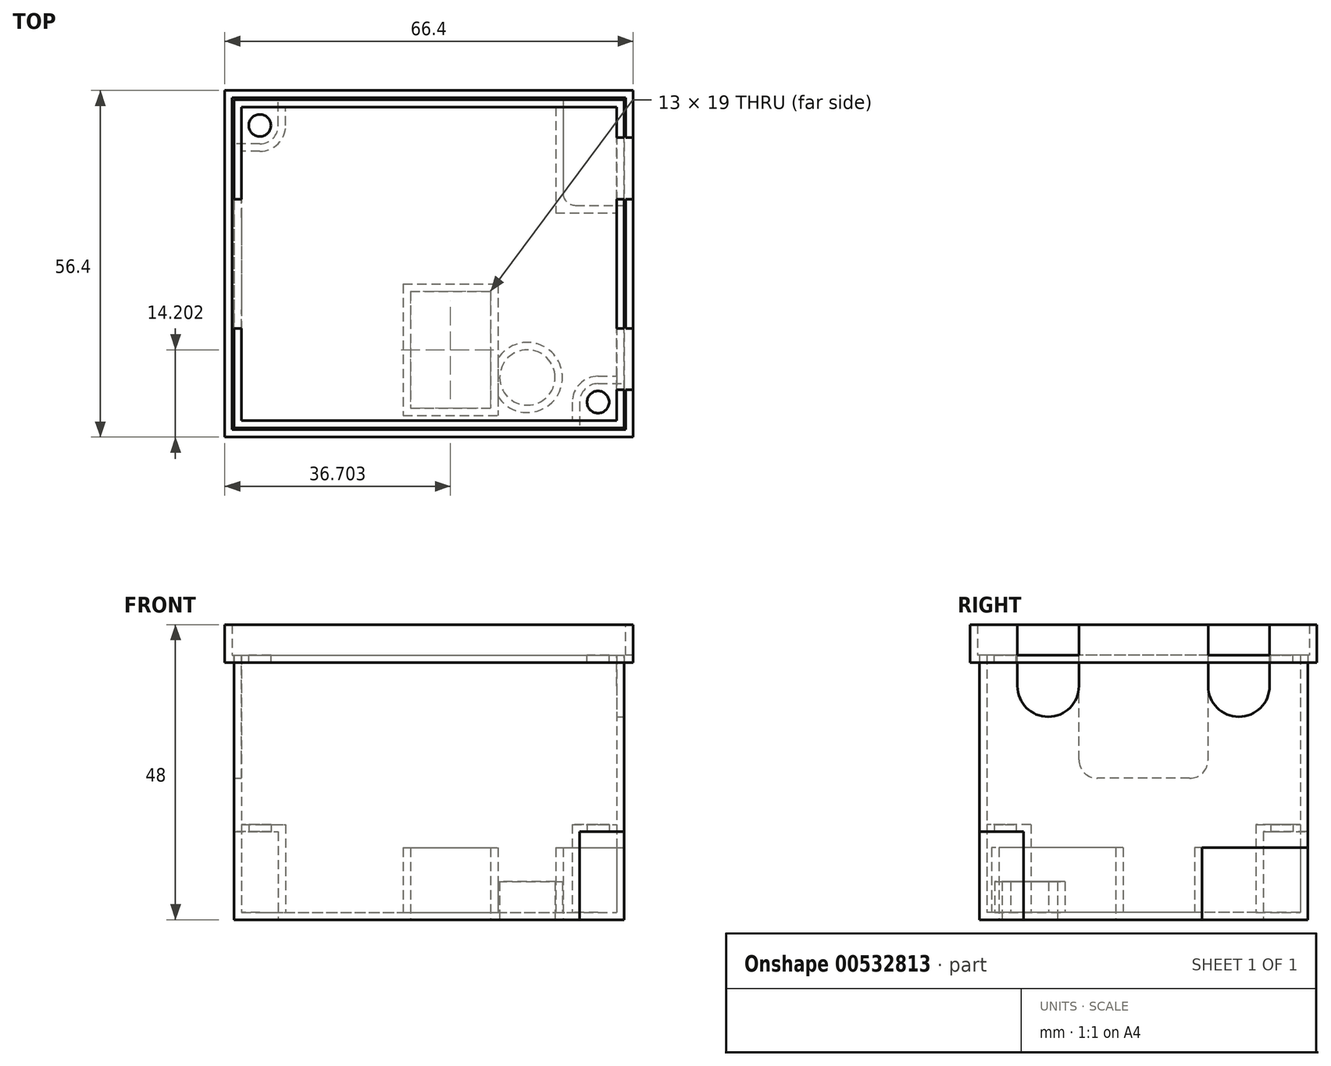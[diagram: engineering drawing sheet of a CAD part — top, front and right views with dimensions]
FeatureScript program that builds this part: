
annotation { "Feature Type Name" : "Feature", "Feature Type Description" : "" }
export const myFeature = defineFeature(function(context is Context, id is Id, definition is map)
    precondition{}
    {
        {
            var Q0;
            Q0=qCreatedBy(makeId("Top.planeOp"),FACE);
            var sketch = newSketch(context, id + "F0", { "sketchPlane" : qUnion([Q0])});
            skLineSegment(sketch, "E0.bottom", {"start": v(-16.96, 26.85) * mm, "end": v(46.44, 26.85) * mm});
            skLineSegment(sketch, "E0.top", {"start": v(-16.96, -26.55) * mm, "end": v(46.44, -26.55) * mm});
            skLineSegment(sketch, "E0.left", {"start": v(-16.96, 26.85) * mm, "end": v(-16.96, -26.55) * mm});
            skLineSegment(sketch, "E0.right", {"start": v(46.44, 26.85) * mm, "end": v(46.44, -26.55) * mm});
            skCircle(sketch, "E1", {"center": v(30.74, -18.35) * mm, "radius": 4.5 * mm});
            skLineSegment(sketch, "E2.bottom", {"start": v(11.74, -4.35) * mm, "end": v(24.74, -4.35) * mm});
            skLineSegment(sketch, "E2.top", {"start": v(11.74, -23.35) * mm, "end": v(24.74, -23.35) * mm});
            skLineSegment(sketch, "E2.left", {"start": v(11.74, -4.35) * mm, "end": v(11.74, -23.35) * mm});
            skLineSegment(sketch, "E2.right", {"start": v(24.74, -4.35) * mm, "end": v(24.74, -23.35) * mm});
            skArc(sketch, "E3", {"start": v(42.24, -19.35) * mm, "mid": v(40.12, -20.23) * mm, "end": v(39.24, -22.35) * mm});
            skArc(sketch, "E4", {"start": v(-12.76, 19.65) * mm, "mid": v(-10.64, 20.53) * mm, "end": v(-9.76, 22.65) * mm});
            skLineSegment(sketch, "E5", {"start": v(-12.76, 19.65) * mm, "end": v(-16.96, 19.65) * mm});
            skLineSegment(sketch, "E6", {"start": v(-9.76, 22.65) * mm, "end": v(-9.76, 26.85) * mm});
            skCircle(sketch, "E7", {"center": v(-12.76, 22.65) * mm, "radius": 1.8 * mm});
            skLineSegment(sketch, "E8", {"start": v(36.54, 26.85) * mm, "end": v(36.54, 9.65) * mm});
            skLineSegment(sketch, "E9", {"start": v(36.54, 9.65) * mm, "end": v(46.44, 9.65) * mm});
            skLineSegment(sketch, "E10", {"start": v(42.24, -19.35) * mm, "end": v(46.44, -19.35) * mm});
            skLineSegment(sketch, "E11", {"start": v(39.24, -22.35) * mm, "end": v(39.24, -26.55) * mm});
            skCircle(sketch, "E12", {"center": v(42.24, -22.35) * mm, "radius": 1.8 * mm});
            skSolve(sketch);
        }
        {
            var Q0;
            Q0=makeQuery(id+"F0.imprint","IMPRINT",FACE,{"disambiguationData":[TD([[makeQuery(id+"F0.imprint","IMPRINT",EDGE,{"derivedFrom":sQuery(id+"F0.wireOp",EDGE,"E0.bottom")}),-1.0]])]});
            var Q1;
            Q1=makeQuery(id+"F0.imprint","IMPRINT",FACE,{"disambiguationData":[TD([[makeQuery(id+"F0.imprint","IMPRINT",EDGE,{"derivedFrom":sQuery(id+"F0.wireOp",EDGE,"9tdKmkdn-hE9F-qVrS-l7sH-JdWV1MObEDVF.bottom")}),-1.0]])]});
            var Q2;
            Q2=makeQuery(id+"F0.imprint","IMPRINT",FACE,{"disambiguationData":[TD([[makeQuery(id+"F0.imprint","IMPRINT",EDGE,{"derivedFrom":sQuery(id+"F0.wireOp",EDGE,"E2.bottom")}),-1.0]])]});
            var Q3;
            Q3=makeQuery(id+"F0.imprint","IMPRINT",FACE,{"disambiguationData":[TD([[makeQuery(id+"F0.imprint","IMPRINT",EDGE,{"derivedFrom":sQuery(id+"F0.wireOp",EDGE,"E1")}),1.0]])]});
            var Q4;
            Q4=makeQuery(id+"F0.imprint","IMPRINT",FACE,{"disambiguationData":[TD([[makeQuery(id+"F0.imprint","IMPRINT",EDGE,{"derivedFrom":sQuery(id+"F0.wireOp",EDGE,"E4")}),1.0]])]});
            var Q5;
            Q5=makeQuery(id+"F0.imprint","IMPRINT",FACE,{"disambiguationData":[TD([[makeQuery(id+"F0.imprint","IMPRINT",EDGE,{"derivedFrom":sQuery(id+"F0.wireOp",EDGE,"E3")}),1.0]])]});
            var Q6;
            Q6=makeQuery(id+"F0.imprint","IMPRINT",FACE,{"disambiguationData":[TD([[makeQuery(id+"F0.imprint","IMPRINT",EDGE,{"derivedFrom":sQuery(id+"F0.wireOp",EDGE,"E1")}),-1.0]])]});
            var Q7;
            Q7=makeQuery(id+"F0.imprint","IMPRINT",FACE,{"disambiguationData":[TD([[makeQuery(id+"F0.imprint","IMPRINT",EDGE,{"derivedFrom":sQuery(id+"F0.wireOp",EDGE,"E7")}),1.0]])]});
            var Q8;
            Q8=makeQuery(id+"F0.imprint","IMPRINT",FACE,{"disambiguationData":[TD([[makeQuery(id+"F0.imprint","IMPRINT",EDGE,{"derivedFrom":sQuery(id+"F0.wireOp",EDGE,"E12")}),1.0]])]});
            extrude(context, id + "F1", {"entities" : qUnion([Q0, Q1, Q2, Q3, Q4, Q5, Q6, Q7, Q8]), "depth" : 43 * mm, "offsetDistance" : 25 * mm});
        }
        {
            var Q0;
            Q0=makeQuery(id+"F0.imprint","IMPRINT",FACE,{"disambiguationData":[TD([[makeQuery(id+"F0.imprint","IMPRINT",EDGE,{"derivedFrom":sQuery(id+"F0.wireOp",EDGE,"E2.bottom")}),-1.0]])]});
            extrude(context, id + "F2", {"entities" : qUnion([Q0]), "operationType" : NewBodyOperationType.REMOVE, "depth" : 10.5 * mm, "offsetDistance" : 25 * mm});
        }
        {
            var Q0;
            {var subQ3=sQuery(id+"F0.wireOp",EDGE,"E8");Q0=makeQuery(id+"F0.imprint","IMPRINT",FACE,{"disambiguationData":[TD([[makeQuery(id+"F0.imprint","IMPRINT",EDGE,{"derivedFrom":subQ3}),1.0]])]});}
            extrude(context, id + "F3", {"entities" : qUnion([Q0]), "operationType" : NewBodyOperationType.REMOVE, "depth" : 10.5 * mm, "offsetDistance" : 25 * mm});
        }
        {
            var Q0;
            Q0=makeQuery(id+"F0.imprint","IMPRINT",FACE,{"disambiguationData":[TD([[makeQuery(id+"F0.imprint","IMPRINT",EDGE,{"derivedFrom":sQuery(id+"F0.wireOp",EDGE,"E1")}),1.0]])]});
            extrude(context, id + "F4", {"entities" : qUnion([Q0]), "operationType" : NewBodyOperationType.REMOVE, "depth" : 5 * mm, "offsetDistance" : 25 * mm});
        }
        {
            var Q0;
            Q0=makeQuery(id+"F0.imprint","IMPRINT",FACE,{"disambiguationData":[TD([[makeQuery(id+"F0.imprint","IMPRINT",EDGE,{"derivedFrom":sQuery(id+"F0.wireOp",EDGE,"E3")}),1.0]])]});
            var Q1;
            Q1=makeQuery(id+"F0.imprint","IMPRINT",FACE,{"disambiguationData":[TD([[makeQuery(id+"F0.imprint","IMPRINT",EDGE,{"derivedFrom":sQuery(id+"F0.wireOp",EDGE,"E4")}),1.0]])]});
            var Q2;
            Q2=makeQuery(id+"F0.imprint","IMPRINT",FACE,{"disambiguationData":[TD([[makeQuery(id+"F0.imprint","IMPRINT",EDGE,{"derivedFrom":sQuery(id+"F0.wireOp",EDGE,"E12")}),1.0]])]});
            var Q3;
            Q3=makeQuery(id+"F0.imprint","IMPRINT",FACE,{"disambiguationData":[TD([[makeQuery(id+"F0.imprint","IMPRINT",EDGE,{"derivedFrom":sQuery(id+"F0.wireOp",EDGE,"E7")}),1.0]])]});
            extrude(context, id + "F5", {"entities" : qUnion([Q0, Q1, Q2, Q3]), "operationType" : NewBodyOperationType.REMOVE, "depth" : 14.3 * mm, "offsetDistance" : 25 * mm});
        }
        {
            var Q0;
            Q0=makeQuery(id+"F1.opExtrude","CAP_FACE",FACE,{"disambiguationData":[OSD([sQuery(id+"F0.wireOp",EDGE,"E0.bottom"),sQuery(id+"F0.wireOp",EDGE,"E0.top"),sQuery(id+"F0.wireOp",EDGE,"E0.left"),sQuery(id+"F0.wireOp",EDGE,"E0.right"),sQuery(id+"F0.wireOp",EDGE,"9tdKmkdn-hE9F-qVrS-l7sH-JdWV1MObEDVF.bottom"),sQuery(id+"F0.wireOp",EDGE,"9tdKmkdn-hE9F-qVrS-l7sH-JdWV1MObEDVF.left")])],"isStart":false});
            shell(context, id + "F6", {"entities" : qUnion([Q0]), "thickness" : 1.2 * mm});
        }
        {
            var Q0;
            Q0=makeQuery(id+"F3.boolean.opBoolean","COPY",FACE,{"derivedFrom":makeQuery(id+"F3.opExtrude","CAP_FACE",FACE,{"disambiguationData":[OSD([sQuery(id+"F0.wireOp",EDGE,"E0.bottom"),sQuery(id+"F0.wireOp",EDGE,"E0.right"),sQuery(id+"F0.wireOp",EDGE,"E8"),sQuery(id+"F0.wireOp",EDGE,"E9")])],"isStart":false})});
            extrude(context, id + "F7", {"entities" : qUnion([Q0]), "operationType" : NewBodyOperationType.REMOVE, "oppositeDirection" : true, "depth" : 1.2 * mm, "offsetDistance" : 25 * mm});
        }
        {
            var Q0;
            {var subQ0=sQuery(id+"F0.wireOp",EDGE,"E9");var subQ1=sQuery(id+"F0.wireOp",EDGE,"E8");Q0=makeQuery(id+"F7.boolean.opBoolean","MERGE",EDGE,{"derivedFrom":[makeQuery(id+"F3.boolean.opBoolean","COPY",EDGE,{"derivedFrom":makeQuery(id+"F3.opExtrude","SWEPT_EDGE",EDGE,{"disambiguationData":[OSD([subQ1,subQ0])]})}),makeQuery(id+"F7.opExtrude","SWEPT_EDGE",EDGE,{"disambiguationData":[OSD([subQ1,subQ0])]})]});}
            var Q1;
            {var subQ0=sQuery(id+"F0.wireOp",EDGE,"E8");var subQ1=sQuery(id+"F0.wireOp",EDGE,"E0.bottom");Q1=makeQuery(id+"F7.boolean.opBoolean","MERGE",EDGE,{"derivedFrom":[makeQuery(id+"F3.boolean.opBoolean","COPY",EDGE,{"derivedFrom":makeQuery(id+"F3.opExtrude","SWEPT_EDGE",EDGE,{"disambiguationData":[OSD([subQ1,subQ0])]})}),makeQuery(id+"F7.opExtrude","SWEPT_EDGE",EDGE,{"disambiguationData":[OSD([subQ1,subQ0])]})]});}
            var Q2;
            {var subQ0=sQuery(id+"F0.wireOp",EDGE,"E9");var subQ1=sQuery(id+"F0.wireOp",EDGE,"E0.right");Q2=makeQuery(id+"F7.boolean.opBoolean","MERGE",EDGE,{"derivedFrom":[makeQuery(id+"F3.boolean.opBoolean","COPY",EDGE,{"derivedFrom":makeQuery(id+"F3.opExtrude","SWEPT_EDGE",EDGE,{"disambiguationData":[OSD([subQ1,subQ0])]})}),makeQuery(id+"F7.opExtrude","SWEPT_EDGE",EDGE,{"disambiguationData":[OSD([subQ1,subQ0])]})]});}
            fillet(context, id + "F8", {"entities" : qUnion([Q0, Q1, Q2]), "radius" : 2 * mm, "tangentPropagation" : true, "allowEdgeOverflow" : false});
        }
        {
            var Q0;
            Q0=makeQuery(id+"F2.boolean.opBoolean","COPY",FACE,{"derivedFrom":makeQuery(id+"F2.opExtrude","CAP_FACE",FACE,{"disambiguationData":[OSD([sQuery(id+"F0.wireOp",EDGE,"E2.bottom"),sQuery(id+"F0.wireOp",EDGE,"E2.top"),sQuery(id+"F0.wireOp",EDGE,"E2.left"),sQuery(id+"F0.wireOp",EDGE,"E2.right")])],"isStart":false})});
            extrude(context, id + "F9", {"entities" : qUnion([Q0]), "operationType" : NewBodyOperationType.REMOVE, "oppositeDirection" : true, "depth" : 1.2 * mm, "offsetDistance" : 25 * mm});
        }
        {
            var Q0;
            Q0=makeQuery(id+"F4.boolean.opBoolean","COPY",FACE,{"derivedFrom":makeQuery(id+"F4.opExtrude","CAP_FACE",FACE,{"disambiguationData":[OSD([sQuery(id+"F0.wireOp",EDGE,"E1")])],"isStart":false})});
            extrude(context, id + "F10", {"entities" : qUnion([Q0]), "operationType" : NewBodyOperationType.REMOVE, "oppositeDirection" : true, "depth" : 1.2 * mm, "offsetDistance" : 25 * mm});
        }
        {
            var Q0;
            Q0=makeQuery(id+"F0.imprint","IMPRINT",FACE,{"disambiguationData":[TD([[makeQuery(id+"F0.imprint","IMPRINT",EDGE,{"derivedFrom":sQuery(id+"F0.wireOp",EDGE,"E12")}),1.0]])]});
            extrude(context, id + "F11", {"entities" : qUnion([Q0]), "operationType" : NewBodyOperationType.REMOVE, "depth" : 18 * mm, "offsetDistance" : 25 * mm});
        }
        {
            var Q0;
            Q0=makeQuery(id+"F0.imprint","IMPRINT",FACE,{"disambiguationData":[TD([[makeQuery(id+"F0.imprint","IMPRINT",EDGE,{"derivedFrom":sQuery(id+"F0.wireOp",EDGE,"E7")}),1.0]])]});
            extrude(context, id + "F12", {"entities" : qUnion([Q0]), "operationType" : NewBodyOperationType.REMOVE, "depth" : 18 * mm, "offsetDistance" : 25 * mm});
        }
        {
            var Q0;
            Q0=makeQuery(id+"F1.opExtrude","CAP_FACE",FACE,{"disambiguationData":[OSD([sQuery(id+"F0.wireOp",EDGE,"E0.bottom"),sQuery(id+"F0.wireOp",EDGE,"E0.top"),sQuery(id+"F0.wireOp",EDGE,"E0.left"),sQuery(id+"F0.wireOp",EDGE,"E0.right"),sQuery(id+"F0.wireOp",EDGE,"9tdKmkdn-hE9F-qVrS-l7sH-JdWV1MObEDVF.bottom"),sQuery(id+"F0.wireOp",EDGE,"9tdKmkdn-hE9F-qVrS-l7sH-JdWV1MObEDVF.left")])],"isStart":false});
            var sketch = newSketch(context, id + "F13", { "sketchPlane" : qUnion([Q0])});
            skLineSegment(sketch, "E13.0", {"start": v(-15.76, 25.65) * mm, "end": v(45.24, 25.65) * mm});
            skLineSegment(sketch, "E13.1", {"start": v(-15.76, -25.35) * mm, "end": v(45.24, -25.35) * mm});
            skLineSegment(sketch, "E13.2", {"start": v(-16.96, -26.55) * mm, "end": v(46.44, -26.55) * mm});
            skLineSegment(sketch, "E13.3", {"start": v(45.24, 25.65) * mm, "end": v(45.24, -25.35) * mm});
            skLineSegment(sketch, "E13.4", {"start": v(46.44, 26.85) * mm, "end": v(46.44, -26.55) * mm});
            skLineSegment(sketch, "E13.5", {"start": v(-16.96, 26.85) * mm, "end": v(46.44, 26.85) * mm});
            skLineSegment(sketch, "E13.6", {"start": v(-15.76, 25.65) * mm, "end": v(-15.76, -25.35) * mm});
            skLineSegment(sketch, "E13.7", {"start": v(-16.96, 26.85) * mm, "end": v(-16.96, -26.55) * mm});
            skLineSegment(sketch, "E14.bottom", {"start": v(-18.76, 10.65) * mm, "end": v(-12.3, 10.65) * mm});
            skLineSegment(sketch, "E14.top", {"start": v(-18.76, -10.35) * mm, "end": v(-12.3, -10.35) * mm});
            skLineSegment(sketch, "E14.left", {"start": v(-18.76, 10.65) * mm, "end": v(-18.76, -10.35) * mm});
            skLineSegment(sketch, "E14.right", {"start": v(-12.3, 10.65) * mm, "end": v(-12.3, -10.35) * mm});
            skLineSegment(sketch, "E15.bottom", {"start": v(43.62, 20.65) * mm, "end": v(49.6, 20.65) * mm});
            skLineSegment(sketch, "E15.top", {"start": v(43.62, 10.65) * mm, "end": v(49.6, 10.65) * mm});
            skLineSegment(sketch, "E15.left", {"start": v(43.62, 20.65) * mm, "end": v(43.62, 10.65) * mm});
            skLineSegment(sketch, "E15.right", {"start": v(49.6, 20.65) * mm, "end": v(49.6, 10.65) * mm});
            skLineSegment(sketch, "E16.bottom", {"start": v(41.79, -10.35) * mm, "end": v(49.6, -10.35) * mm});
            skLineSegment(sketch, "E16.top", {"start": v(41.79, -20.35) * mm, "end": v(49.6, -20.35) * mm});
            skLineSegment(sketch, "E16.left", {"start": v(41.79, -10.35) * mm, "end": v(41.79, -20.35) * mm});
            skLineSegment(sketch, "E16.right", {"start": v(49.6, -10.35) * mm, "end": v(49.6, -20.35) * mm});
            skSolve(sketch);
        }
        {
            var Q0;
            {var subQ0=sQuery(id+"F13.wireOp",EDGE,"E14.bottom");var subQ1=sQuery(id+"F13.wireOp",EDGE,"E13.6");var subQ2=makeQuery(id+"F13.imprint","INTERSECT",VERTEX,{"derivedFrom":[subQ1,subQ0]});Q0=makeQuery(id+"F13.imprint","IMPRINT",FACE,{"disambiguationData":[TD([[makeQuery(id+"F13.imprint","IMPRINT",EDGE,{"disambiguationData":[TD([[subQ2,-1.0]])],"derivedFrom":subQ1}),-1.0]])]});}
            extrude(context, id + "F14", {"entities" : qUnion([Q0]), "operationType" : NewBodyOperationType.REMOVE, "oppositeDirection" : true, "depth" : 20 * mm, "offsetDistance" : 25 * mm});
        }
        {
            var Q0;
            {var subQ0=sQuery(id+"F13.wireOp",EDGE,"E15.bottom");var subQ1=sQuery(id+"F13.wireOp",EDGE,"E13.3");var subQ2=makeQuery(id+"F13.imprint","INTERSECT",VERTEX,{"derivedFrom":[subQ1,subQ0]});Q0=makeQuery(id+"F13.imprint","IMPRINT",FACE,{"disambiguationData":[TD([[makeQuery(id+"F13.imprint","IMPRINT",EDGE,{"disambiguationData":[TD([[subQ2,-1.0]])],"derivedFrom":subQ1}),1.0]])]});}
            var Q1;
            {var subQ0=sQuery(id+"F13.wireOp",EDGE,"E16.bottom");var subQ1=sQuery(id+"F13.wireOp",EDGE,"E13.3");var subQ2=makeQuery(id+"F13.imprint","INTERSECT",VERTEX,{"derivedFrom":[subQ1,subQ0]});Q1=makeQuery(id+"F13.imprint","IMPRINT",FACE,{"disambiguationData":[TD([[makeQuery(id+"F13.imprint","IMPRINT",EDGE,{"disambiguationData":[TD([[subQ2,-1.0]])],"derivedFrom":subQ1}),1.0]])]});}
            extrude(context, id + "F15", {"entities" : qUnion([Q0, Q1]), "operationType" : NewBodyOperationType.REMOVE, "oppositeDirection" : true, "depth" : 10 * mm, "offsetDistance" : 25 * mm});
        }
        {
            var Q0;
            Q0=makeQuery(id+"F15.boolean.opBoolean","COPY",EDGE,{"derivedFrom":makeQuery(id+"F15.opExtrude","CAP_EDGE",EDGE,{"disambiguationData":[OSD([sQuery(id+"F13.wireOp",EDGE,"E15.top")])],"isStart":false})});
            var Q1;
            Q1=makeQuery(id+"F15.boolean.opBoolean","COPY",EDGE,{"derivedFrom":makeQuery(id+"F15.opExtrude","CAP_EDGE",EDGE,{"disambiguationData":[OSD([sQuery(id+"F13.wireOp",EDGE,"E16.top")])],"isStart":false})});
            var Q2;
            Q2=makeQuery(id+"F15.boolean.opBoolean","COPY",EDGE,{"derivedFrom":makeQuery(id+"F15.opExtrude","CAP_EDGE",EDGE,{"disambiguationData":[OSD([sQuery(id+"F13.wireOp",EDGE,"E15.bottom")])],"isStart":false})});
            var Q3;
            Q3=makeQuery(id+"F15.boolean.opBoolean","COPY",EDGE,{"derivedFrom":makeQuery(id+"F15.opExtrude","CAP_EDGE",EDGE,{"disambiguationData":[OSD([sQuery(id+"F13.wireOp",EDGE,"E16.bottom")])],"isStart":false})});
            fillet(context, id + "F16", {"entities" : qUnion([Q0, Q1, Q2, Q3]), "radius" : 5 * mm, "tangentPropagation" : true, "allowEdgeOverflow" : false});
        }
        {
            var Q0;
            Q0=makeQuery(id+"F14.boolean.opBoolean","COPY",EDGE,{"derivedFrom":makeQuery(id+"F14.opExtrude","CAP_EDGE",EDGE,{"disambiguationData":[OSD([sQuery(id+"F13.wireOp",EDGE,"E14.bottom")])],"isStart":false})});
            var Q1;
            Q1=makeQuery(id+"F14.boolean.opBoolean","COPY",EDGE,{"derivedFrom":makeQuery(id+"F14.opExtrude","CAP_EDGE",EDGE,{"disambiguationData":[OSD([sQuery(id+"F13.wireOp",EDGE,"E14.top")])],"isStart":false})});
            fillet(context, id + "F17", {"entities" : qUnion([Q0, Q1]), "radius" : 3 * mm, "tangentPropagation" : true, "allowEdgeOverflow" : false});
        }
        {
            var Q0;
            {var subQ0=sQuery(id+"F0.wireOp",EDGE,"E0.right");Q0=makeQuery(id+"F15.boolean.opBoolean","SPLIT",FACE,{"disambiguationData":[TD([makeQuery(id+"F15.opExtrude","SWEPT_FACE",FACE,{"disambiguationData":[OSD([sQuery(id+"F13.wireOp",EDGE,"E15.top")])]})])],"derivedFrom":makeQuery(id+"F1.opExtrude","CAP_FACE",FACE,{"disambiguationData":[OSD([sQuery(id+"F0.wireOp",EDGE,"E0.bottom"),sQuery(id+"F0.wireOp",EDGE,"E0.top"),sQuery(id+"F0.wireOp",EDGE,"E0.left"),subQ0])],"isStart":false})});}
            var sketch = newSketch(context, id + "F18", { "sketchPlane" : qUnion([Q0])});
            skLineSegment(sketch, "E17.0", {"start": v(-16.96, 26.85) * mm, "end": v(-16.96, 10.65) * mm, "construction": true});
            skLineSegment(sketch, "E17.1", {"start": v(-16.96, 26.85) * mm, "end": v(46.44, 26.85) * mm, "construction": true});
            skLineSegment(sketch, "E17.2", {"start": v(46.44, 26.85) * mm, "end": v(46.44, 20.65) * mm, "construction": true});
            skLineSegment(sketch, "E17.3", {"start": v(46.44, 10.65) * mm, "end": v(46.44, -10.35) * mm, "construction": true});
            skLineSegment(sketch, "E17.4", {"start": v(-16.96, -26.55) * mm, "end": v(46.44, -26.55) * mm, "construction": true});
            skLineSegment(sketch, "E17.5", {"start": v(46.44, -20.35) * mm, "end": v(46.44, -26.55) * mm, "construction": true});
            skLineSegment(sketch, "E17.6", {"start": v(-16.96, -10.35) * mm, "end": v(-16.96, -26.55) * mm, "construction": true});
            skCircle(sketch, "E18.0", {"center": v(-12.76, 22.65) * mm, "radius": 1.8 * mm});
            skCircle(sketch, "E18.1", {"center": v(42.24, -22.35) * mm, "radius": 1.8 * mm});
            skLineSegment(sketch, "E19.bottom", {"start": v(-17.26, 27.15) * mm, "end": v(46.74, 27.15) * mm});
            skLineSegment(sketch, "E19.top", {"start": v(-17.26, -26.85) * mm, "end": v(46.74, -26.85) * mm});
            skLineSegment(sketch, "E19.left", {"start": v(-17.26, 27.15) * mm, "end": v(-17.26, -26.85) * mm});
            skLineSegment(sketch, "E19.right", {"start": v(46.74, 27.15) * mm, "end": v(46.74, -26.85) * mm});
            skSolve(sketch);
        }
        {
            var Q0;
            Q0=makeQuery(id+"F18.imprint","IMPRINT",FACE,{"disambiguationData":[TD([[makeQuery(id+"F18.imprint","IMPRINT",EDGE,{"derivedFrom":sQuery(id+"F18.wireOp",EDGE,"E18.0")}),-1.0]])]});
            var Q1;
            {var subQ0=sQuery(id+"F13.wireOp",EDGE,"E15.top");Q1=makeQuery(id+"F18.imprint","IMPRINT",FACE,{"disambiguationData":[TD([[makeQuery(id+"F18.imprint","IMPRINT",EDGE,{"derivedFrom":makeQuery(id+"F15.boolean.opBoolean","COPY",EDGE,{"derivedFrom":makeQuery(id+"F15.opExtrude","CAP_EDGE",EDGE,{"disambiguationData":[OSD([subQ0])],"isStart":true})})}),-1.0]])]});}
            var Q2;
            Q2=makeQuery(id+"F18.imprint","IMPRINT",FACE,{"disambiguationData":[TD([[makeQuery(id+"F18.imprint","IMPRINT",EDGE,{"derivedFrom":sQuery(id+"F18.wireOp",EDGE,"E18.1")}),1.0]])]});
            var Q3;
            Q3=makeQuery(id+"F18.imprint","IMPRINT",FACE,{"disambiguationData":[TD([[makeQuery(id+"F18.imprint","IMPRINT",EDGE,{"derivedFrom":sQuery(id+"F18.wireOp",EDGE,"E18.0")}),1.0]])]});
            extrude(context, id + "F19", {"entities" : qUnion([Q0, Q1, Q2, Q3]), "depth" : 5 * mm, "offsetDistance" : 25 * mm});
        }
        {
            var Q0;
            Q0=makeQuery(id+"F19.opExtrude","CAP_FACE",FACE,{"disambiguationData":[OSD([sQuery(id+"F18.wireOp",EDGE,"E18.0"),sQuery(id+"F18.wireOp",EDGE,"E18.1"),sQuery(id+"F18.wireOp",EDGE,"E19.bottom"),sQuery(id+"F18.wireOp",EDGE,"E19.top"),sQuery(id+"F18.wireOp",EDGE,"E19.left"),sQuery(id+"F18.wireOp",EDGE,"E19.right")])],"isStart":false});
            shell(context, id + "F20", {"entities" : qUnion([Q0]), "thickness" : 1.2 * mm, "oppositeDirection" : true});
        }
        {
            var Q0;
            Q0=makeQuery(id+"F18.imprint","IMPRINT",FACE,{"disambiguationData":[TD([[makeQuery(id+"F18.imprint","IMPRINT",EDGE,{"derivedFrom":sQuery(id+"F18.wireOp",EDGE,"E18.0")}),1.0]])]});
            var Q1;
            Q1=makeQuery(id+"F18.imprint","IMPRINT",FACE,{"disambiguationData":[TD([[makeQuery(id+"F18.imprint","IMPRINT",EDGE,{"derivedFrom":sQuery(id+"F18.wireOp",EDGE,"E18.1")}),1.0]])]});
            extrude(context, id + "F21", {"entities" : qUnion([Q0, Q1]), "operationType" : NewBodyOperationType.REMOVE, "oppositeDirection" : true, "depth" : 1.2 * mm, "offsetDistance" : 25 * mm});
        }
        {
            var Q0;
            Q0=makeQuery(id+"F19.opExtrude","CAP_FACE",FACE,{"disambiguationData":[OSD([sQuery(id+"F18.wireOp",EDGE,"E19.bottom"),sQuery(id+"F18.wireOp",EDGE,"E19.top"),sQuery(id+"F18.wireOp",EDGE,"E19.left"),sQuery(id+"F18.wireOp",EDGE,"E19.right")])],"isStart":false});
            var sketch = newSketch(context, id + "F22", { "sketchPlane" : qUnion([Q0])});
            skPoint(sketch, "E20.4", {"position": v(45.84, 20.65) * mm});
            skLineSegment(sketch, "E21", {"start": v(46.74, 20.65) * mm, "end": v(47.94, 20.65) * mm});
            skLineSegment(sketch, "E22", {"start": v(47.94, 10.65) * mm, "end": v(46.74, 10.65) * mm});
            skLineSegment(sketch, "E23", {"start": v(46.74, -10.35) * mm, "end": v(47.94, -10.35) * mm});
            skLineSegment(sketch, "E24", {"start": v(47.94, -20.35) * mm, "end": v(46.74, -20.35) * mm});
            skLineSegment(sketch, "E25.0", {"start": v(47.94, 28.35) * mm, "end": v(47.94, -28.05) * mm});
            skLineSegment(sketch, "E25.1", {"start": v(46.74, 27.15) * mm, "end": v(46.74, -26.85) * mm});
            skPoint(sketch, "E26.orphan", {"position": v(49.53, 10.65) * mm});
            skPoint(sketch, "E20.1.end.orphan", {"position": v(46.44, 10.65) * mm});
            skPoint(sketch, "E20.1.start.orphan", {"position": v(45.24, 10.65) * mm});
            skPoint(sketch, "E27.orphan", {"position": v(45.24, 20.65) * mm});
            skPoint(sketch, "E20.0.end.orphan", {"position": v(46.44, 20.65) * mm});
            skPoint(sketch, "E28.orphan", {"position": v(49.59, -20.35) * mm});
            skPoint(sketch, "E20.2.start.orphan", {"position": v(45.24, -10.35) * mm});
            skPoint(sketch, "E20.3.start.orphan", {"position": v(45.24, -20.35) * mm});
            skPoint(sketch, "E29.orphan", {"position": v(46.44, -20.35) * mm});
            skPoint(sketch, "E30.orphan", {"position": v(46.44, -10.35) * mm});
            skSolve(sketch);
        }
        {
            var Q0;
            {var subQ0=sQuery(id+"F22.wireOp",EDGE,"E23");Q0=makeQuery(id+"F22.imprint","IMPRINT",FACE,{"disambiguationData":[TD([[makeQuery(id+"F22.imprint","IMPRINT",EDGE,{"derivedFrom":subQ0}),-1.0]])]});}
            var Q1;
            {var subQ0=sQuery(id+"F22.wireOp",EDGE,"E21");Q1=makeQuery(id+"F22.imprint","IMPRINT",FACE,{"disambiguationData":[TD([[makeQuery(id+"F22.imprint","IMPRINT",EDGE,{"derivedFrom":subQ0}),-1.0]])]});}
            extrude(context, id + "F23", {"entities" : qUnion([Q0, Q1]), "operationType" : NewBodyOperationType.REMOVE, "oppositeDirection" : true, "depth" : 5 * mm, "offsetDistance" : 25 * mm});
        }
    });
